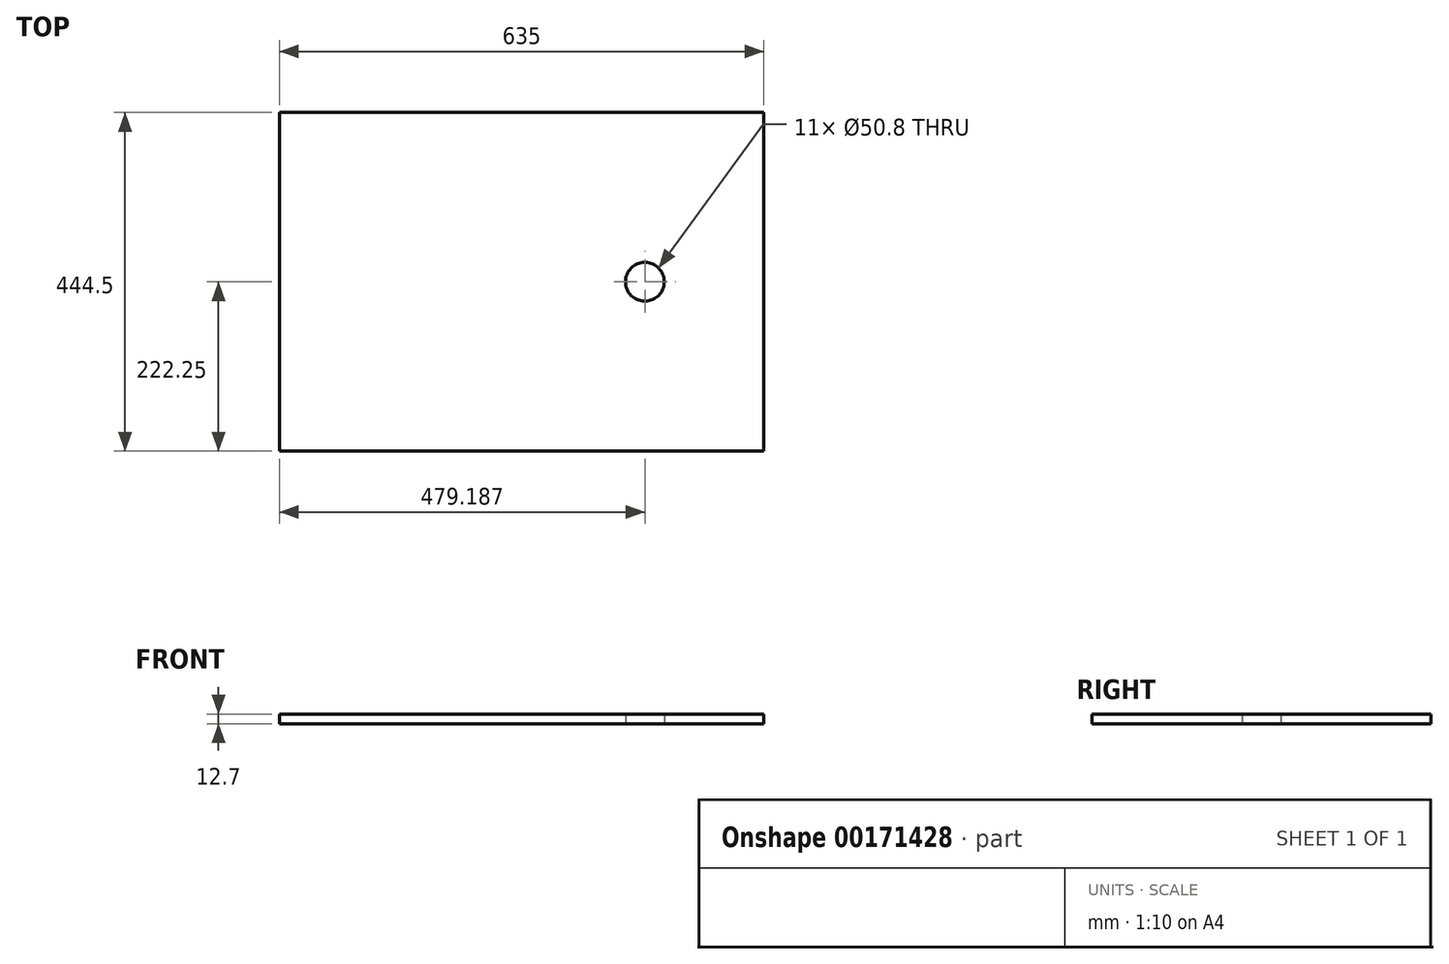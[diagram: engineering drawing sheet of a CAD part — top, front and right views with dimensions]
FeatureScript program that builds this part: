
annotation { "Feature Type Name" : "Feature", "Feature Type Description" : "" }
export const myFeature = defineFeature(function(context is Context, id is Id, definition is map)
    precondition{}
    {
        {
            var Q0;
            Q0=qCreatedBy(makeId("Top.planeOp"),FACE);
            var sketch = newSketch(context, id + "F0", { "sketchPlane" : qUnion([Q0])});
            skLineSegment(sketch, "E0.bottom", {"start": v(-317.5, 222.25) * mm, "end": v(317.5, 222.25) * mm});
            skLineSegment(sketch, "E0.top", {"start": v(-317.5, -222.25) * mm, "end": v(317.5, -222.25) * mm});
            skLineSegment(sketch, "E0.left", {"start": v(-317.5, 222.25) * mm, "end": v(-317.5, -222.25) * mm});
            skLineSegment(sketch, "E0.right", {"start": v(317.5, 222.25) * mm, "end": v(317.5, -222.25) * mm});
            skPoint(sketch, "E0.middle", {"position": v(0, 0) * mm});
            skCircle(sketch, "E1", {"center": v(161.69, 0) * mm, "radius": 25.4 * mm});
            skSolve(sketch);
        }
        {
            var Q0;
            Q0 = qSketchRegion(id + "F0", true);
            var Q1;
            Q1=makeQuery(id+"F0.imprint","IMPRINT",FACE,{"disambiguationData":[TD([[makeQuery(id+"F0.imprint","IMPRINT",EDGE,{"derivedFrom":sQuery(id+"F0.wireOp",EDGE,"E1")}),1.0]])]});
            extrude(context, id + "F1", {"entities" : qUnion([Q0, Q1]), "depth" : 12.7 * mm});
        }
        {
            var Q0;
            Q0=makeQuery(id+"F0.imprint","IMPRINT",FACE,{"disambiguationData":[TD([[makeQuery(id+"F0.imprint","IMPRINT",EDGE,{"derivedFrom":sQuery(id+"F0.wireOp",EDGE,"E1")}),1.0]])]});
            extrude(context, id + "F2", {"entities" : qUnion([Q0]), "operationType" : NewBodyOperationType.REMOVE, "depth" : 25.4 * mm});
        }
    });
